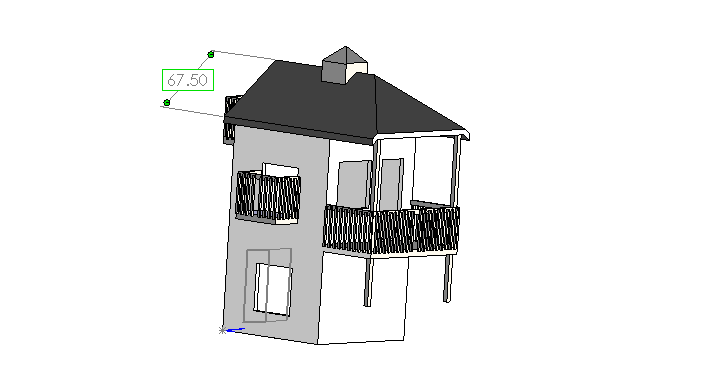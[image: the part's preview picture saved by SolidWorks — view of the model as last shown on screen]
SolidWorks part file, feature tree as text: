
SOLIDWORKS PART (.sldprt)
format: sldprt  version: not decoded by parser v0  size: 1,359,872 bytes
history: native  units: mm
features: sketch x22, extrude x16, plane x10, cut_extrude x5, chamfer x4, shell x1 + 1 further entry (+10 scaffold rows collapsed)
feature tree (69):
  "Annotations"  RD1=1714.5mm
  scaffold x10  (default folders/planes/origin — collapsed)
  sketch  "Sketch1"  dims[D1=2438.4mm D2=2438.4mm]
  extrude  "Extrude1"  Depth=4064mm
  sketch  "Sketch2"  dims[D1=914.4mm]
  extrude  "Extrude2"  Depth=1219.2mm
  shell  "Shell1"  Thickness=88.9mm
  sketch  "Sketch3"  dims[D1=152.4mm D2=152.4mm D3=101.6mm]
  extrude  "Extrude3"  Depth=152.4mm
  plane  "Base"  Offset=2.54mm
  plane  "FirstFloor"  Offset=190.5mm
  plane  "SecondFloor"  Offset=1727.2mm
  plane  "LoftFloor"  Offset=1676.4mm
  sketch  "Sketch4"  dims[D1=139.7mm]
  extrude  "Extrude4"  Depth=1219.2mm
  sketch  "Sketch5"  dims[D1=914.4mm D2=762.0mm D3=914.4mm D4=457.2mm]
  cut_extrude  "Cut-Extrude1"  Depth=127mm
  sketch  "Sketch6"  dims[D1=139.7mm D2=1219.2mm D3=609.6mm]
  extrude  "Extrude5"  Depth=812.8mm
  sketch  "Sketch7"  dims[D1=609.6mm D2=304.8mm D3=38.1mm D4=1524.0mm D5=304.8mm D6=914.4mm]
  cut_extrude  "Cut-Extrude2"  Depth=127mm
  sketch  "Sketch8"  dims[c1.D1=1371.6mm c1.D2=406.4mm c1.D3=406.4mm c2.D2=609.6mm c2.D3=127.0mm]
  sketch  "Sketch9"  dims[D1=457.2mm D2=914.4mm D3=762.0mm]
  cut_extrude  "Cut-Extrude3"  Depth=127mm
  sketch  "Sketch11"  dims[D1=88.9mm D2=38.1mm D3=38.1mm D4=38.1mm]
  extrude  "Extrude6"  [1 undecoded]
  plane  "RailingTop"  Offset=762mm
  sketch  "Sketch13"  dims[D1=38.1mm D2=38.1mm D3=38.1mm]
  extrude  "Extrude7"  Depth=88.9mm
  sketch  "Sketch17"  dims[D1=38.1mm D2=38.1mm D3=38.1mm D4=38.1mm D5=127.0mm]
  extrude  "Extrude8"  Depth=736.6mm
  plane  "Plane6"  Offset=762mm
  sketch  "Sketch18"  dims[D1=38.1mm D2=38.1mm D3=38.1mm]
  extrude  "Extrude9"  Depth=88.9mm
  sketch  "Sketch20"  dims[D1=38.1mm D2=38.1mm D3=38.1mm D4=38.1mm]
  extrude  "Extrude10"  Depth=736.6mm
  plane  "Plane7"  Offset=508mm
  sketch  "Sketch21"  dims[c1.D1=609.6mm c1.D2=152.4mm c1.D3=1524.0mm c2.D2=1219.2mm c2.D3=304.8mm]
  extrude  "Extrude11"  Depth=711.2mm
  chamfer  "Chamfer1"  Distance=304.8mm Angle=45deg
  chamfer  "Chamfer2"  Distance=304.8mm Angle=45deg
  chamfer  "Chamfer8"  Distance=406.4mm
  chamfer  "Chamfer9"  Distance=406.4mm
  sketch  "Sketch23"  dims[D1=88.9mm]
  extrude  "Extrude12"  Depth=914.4mm
  plane  "Plane8"  Offset=508mm
  sketch  "Sketch24"
  cut_extrude  "Cut-Extrude5"  Depth=3048mm
  sketch  "Sketch25"  dims[D1=139.7mm D2=1016.0mm D3=50.8mm]
  extrude  "Extrude13"  Depth=609.6mm
  plane  "Plane9"  Offset=762mm
  sketch  "Sketch27"  dims[c1.D1=38.1mm c1.D2=38.1mm c1.D3=38.1mm c2.D1=38.1mm c2.D2=38.1mm]
  extrude  "Extrude14"  Depth=88.9mm
  sketch  "Sketch28"  dims[D1=38.1mm D2=38.1mm]
  extrude  "Extrude15"  Depth=736.6mm
  plane  "Plane10"  Offset=436.88mm
  sketch  "Sketch29"
  extrude  "Extrude16"  Depth=76.2mm
  sketch  "Sketch30"  dims[D1=914.4mm D2=457.2mm D3=762.0mm]
  cut_extrude  "Cut-Extrude6"  Depth=127mm
decode coverage: 45 of 48 modeling features carry decoded parameters; 1 rows unclassified (native names shown)
note: 1 parameter value undecoded
note: suppression state not decoded; provenance and decode notes live in map.json
